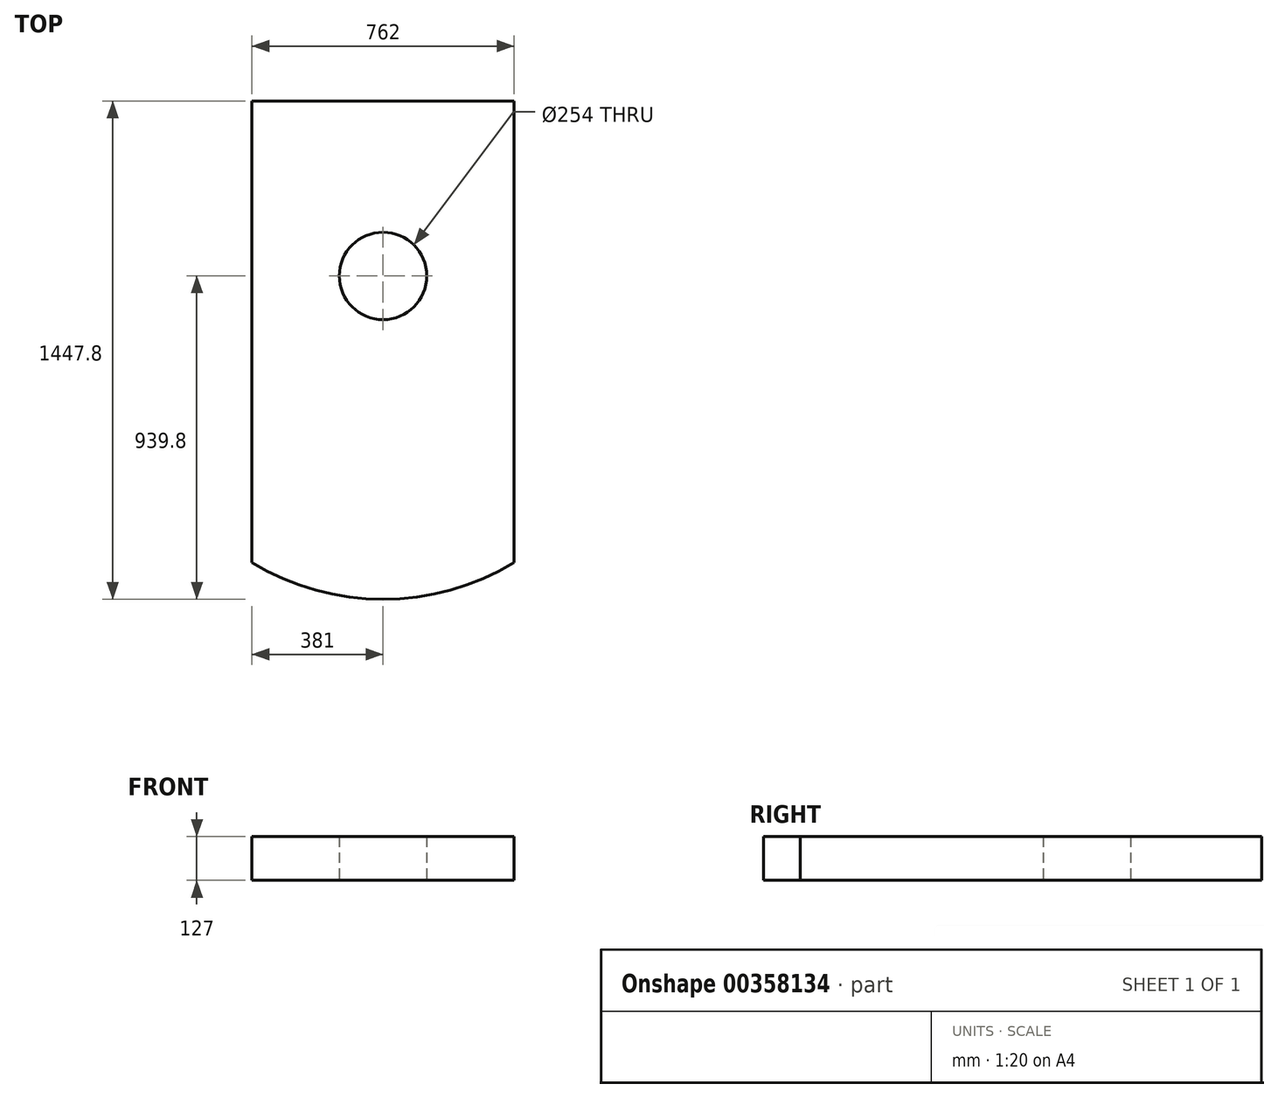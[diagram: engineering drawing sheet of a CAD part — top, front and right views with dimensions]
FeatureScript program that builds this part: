
annotation { "Feature Type Name" : "Feature", "Feature Type Description" : "" }
export const myFeature = defineFeature(function(context is Context, id is Id, definition is map)
    precondition{}
    {
        {
            var Q0;
            Q0=qCreatedBy(makeId("Top.planeOp"),FACE);
            var sketch = newSketch(context, id + "F0", { "sketchPlane" : qUnion([Q0])});
            skCircle(sketch, "E0", {"center": v(0, 0) * mm, "radius": 127 * mm});
            skLineSegment(sketch, "E1", {"start": v(-381, 0) * mm, "end": v(-381, 508) * mm});
            skLineSegment(sketch, "E2", {"start": v(-381, 508) * mm, "end": v(381, 508) * mm});
            skLineSegment(sketch, "E3", {"start": v(381, 508) * mm, "end": v(381, 0) * mm});
            skLineSegment(sketch, "E4", {"start": v(381, 0) * mm, "end": v(381, -833.61) * mm});
            skLineSegment(sketch, "E5", {"start": v(-381, 0) * mm, "end": v(-381, -833.61) * mm});
            skArc(sketch, "E6", {"start": v(-381, -833.61) * mm, "mid": v(0, -939.8) * mm, "end": v(381, -833.61) * mm});
            skSolve(sketch);
        }
        {
            var Q0;
            Q0 = qSketchRegion(id + "F0", true);
            extrude(context, id + "F1", {"entities" : qUnion([Q0]), "depth" : 127 * mm});
        }
    });
